# Revit family: Bernhardt_Design-Tables-Freestanding-Arched-Blueprint
name_source: partatom
category: Furniture
revit_build: Autodesk Revit 2016 (Build: 20150714_1515(x64)
units: mm (PartAtom-declared; Revit-internal decimal feet)

## family parameters
Always vertical = Yes
Cut with Voids When Loaded = No
OmniClass Number = 23.40.20.00
OmniClass Title = General Furniture and Specialties
Room Calculation Point = No
Shared = No
Work Plane-Based = No

## types (2) — shared parameters
BlackPaint = Black Paint
Manufacturer = Bernhardt Design
Model = Blueprint
TableTop = <By Category>
TableTopHeight = 2' - 4 3/4"
TotalHeight = 2' - 6"
URL = http://www.bernhardtdesign.com
Wood = <By Category>

## per-type parameters (varying)
| type | Arched_large | Arched_small | Crossbar_bottom | Crossbar_top | Legs_large | Legs_small | PlateRadius | RoundRadius | Support_large | Support_small |
| BPS-YAA-AA000 | No | Yes | -1' - 0 1/16" | 1' - 0 1/16" | No | Yes | 0' - 11 13/16" | 2' - 3" | No | Yes |
| BPS-YDD-AA000 | Yes | No | -1' - 5" | 1' - 5" | Yes | No | 1' - 7 3/4" | 2' - 6" | Yes | No |

note: column(s) folded — value = type name in every type: Catalog, SKU

## geometry (parser evidence)
native form markers: Sweep x2
no freeform markers — native parametric forms only
